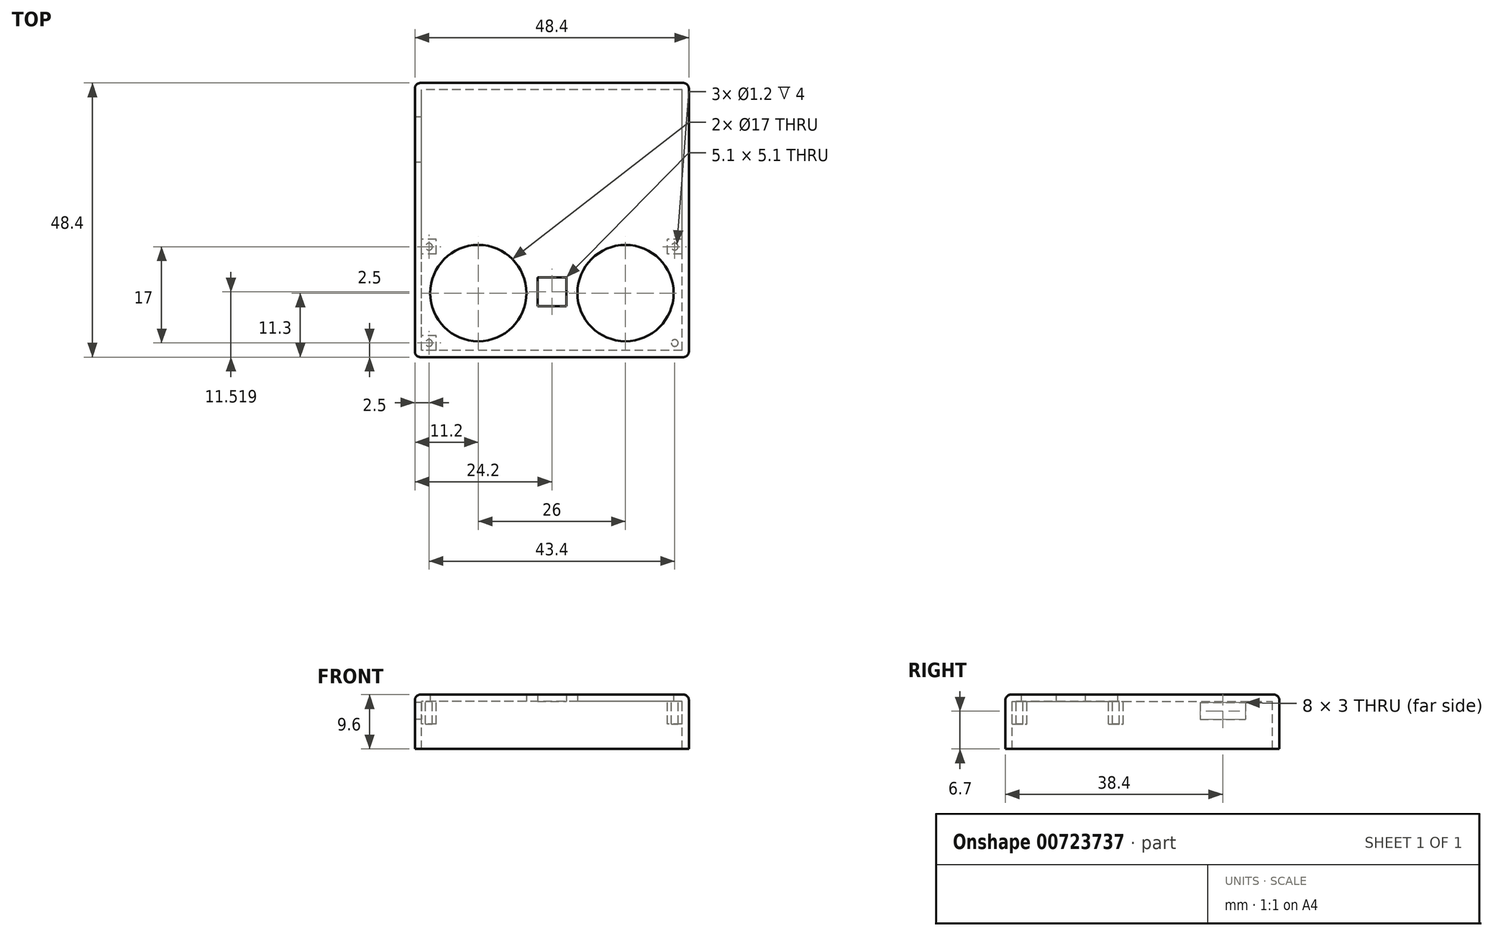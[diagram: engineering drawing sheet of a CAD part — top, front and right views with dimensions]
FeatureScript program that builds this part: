
annotation { "Feature Type Name" : "Feature", "Feature Type Description" : "" }
export const myFeature = defineFeature(function(context is Context, id is Id, definition is map)
    precondition{}
    {
        {
            var Q0;
            Q0=qCreatedBy(makeId("Top.planeOp"),FACE);
            var sketch = newSketch(context, id + "F0", { "sketchPlane" : qUnion([Q0])});
            skLineSegment(sketch, "E0.bottom", {"start": v(0, 0) * mm, "end": v(-23, 0) * mm});
            skLineSegment(sketch, "E0.top", {"start": v(0, 23) * mm, "end": v(-23, 23) * mm});
            skLineSegment(sketch, "E0.left", {"start": v(0, 0) * mm, "end": v(0, 23) * mm});
            skLineSegment(sketch, "E0.right", {"start": v(-23, 0) * mm, "end": v(-23, 23) * mm});
            skLineSegment(sketch, "E1.MirrorCS", {"start": v(-23, 0) * mm, "end": v(-23, -23) * mm});
            skLineSegment(sketch, "E2.MirrorCS", {"start": v(0, 0) * mm, "end": v(0, -23) * mm});
            skLineSegment(sketch, "E3.MirrorCS", {"start": v(0, -23) * mm, "end": v(-23, -23) * mm});
            skLineSegment(sketch, "E4.MirrorCS", {"start": v(0, 23) * mm, "end": v(23, 23) * mm});
            skLineSegment(sketch, "E5.MirrorCS", {"start": v(0, -23) * mm, "end": v(23, -23) * mm});
            skLineSegment(sketch, "E6.MirrorCS", {"start": v(23, 0) * mm, "end": v(23, 23) * mm});
            skLineSegment(sketch, "E7.MirrorCS", {"start": v(0, 0) * mm, "end": v(23, 0) * mm});
            skLineSegment(sketch, "E8.MirrorCS", {"start": v(23, 0) * mm, "end": v(23, -23) * mm});
            skCircle(sketch, "E9", {"center": v(13, -12.9) * mm, "radius": 8.5 * mm});
            skCircle(sketch, "E10", {"center": v(-13, -12.9) * mm, "radius": 8.5 * mm});
            skLineSegment(sketch, "E11.bottom", {"start": v(-2.55, -15.23) * mm, "end": v(2.55, -15.23) * mm});
            skLineSegment(sketch, "E11.top", {"start": v(-2.55, -10.13) * mm, "end": v(2.55, -10.13) * mm});
            skLineSegment(sketch, "E11.left", {"start": v(-2.55, -15.23) * mm, "end": v(-2.55, -10.13) * mm});
            skLineSegment(sketch, "E11.right", {"start": v(2.55, -15.23) * mm, "end": v(2.55, -10.13) * mm});
            skSolve(sketch);
        }
        {
            var Q0;
            {var subQ1=sQuery(id+"F0.wireOp",EDGE,"E0.top");Q0=makeQuery(id+"F0.imprint","IMPRINT",FACE,{"disambiguationData":[TD([[makeQuery(id+"F0.imprint","IMPRINT",EDGE,{"derivedFrom":subQ1}),1.0]])]});}
            var Q1;
            {var subQ1=sQuery(id+"F0.wireOp",EDGE,"E1.MirrorCS");Q1=makeQuery(id+"F0.imprint","IMPRINT",FACE,{"disambiguationData":[TD([[makeQuery(id+"F0.imprint","IMPRINT",EDGE,{"derivedFrom":subQ1}),1.0]])]});}
            var Q2;
            {var subQ7=sQuery(id+"F0.wireOp",EDGE,"E4.MirrorCS");Q2=makeQuery(id+"F0.imprint","IMPRINT",FACE,{"disambiguationData":[TD([[makeQuery(id+"F0.imprint","IMPRINT",EDGE,{"derivedFrom":subQ7}),-1.0]])]});}
            var Q3;
            {var subQ9=sQuery(id+"F0.wireOp",EDGE,"E5.MirrorCS");Q3=makeQuery(id+"F0.imprint","IMPRINT",FACE,{"disambiguationData":[TD([[makeQuery(id+"F0.imprint","IMPRINT",EDGE,{"derivedFrom":subQ9}),1.0]])]});}
            extrude(context, id + "F1", {"entities" : qUnion([Q0, Q1, Q2, Q3]), "endBound" : BoundingType.SYMMETRIC, "depth" : 1.2 * mm, "offsetDistance" : 25 * mm});
        }
        {
            var Q0;
            Q0=makeQuery(id+"F1.opExtrude","CAP_FACE",FACE,{"disambiguationData":[OSD([sQuery(id+"F0.wireOp",EDGE,"E0.top"),sQuery(id+"F0.wireOp",EDGE,"E0.right"),sQuery(id+"F0.wireOp",EDGE,"E1.MirrorCS"),sQuery(id+"F0.wireOp",EDGE,"E3.MirrorCS"),sQuery(id+"F0.wireOp",EDGE,"18OHl2Td-8SmV-nLja-3BuC-y3GKfxBrHoTz"),sQuery(id+"F0.wireOp",EDGE,"E4.MirrorCS"),sQuery(id+"F0.wireOp",EDGE,"f96b6ea1-77e4-4928-808a-502d4fa3524e1.MirrorC"),sQuery(id+"F0.wireOp",EDGE,"E5.MirrorCS"),sQuery(id+"F0.wireOp",EDGE,"E6.MirrorCS"),sQuery(id+"F0.wireOp",EDGE,"E8.MirrorCS"),sQuery(id+"F0.wireOp",EDGE,"ZzQ9hNgQ-oA48-EWd8-CxiW-ZcLfL0NBcqYF")])],"isStart":false});
            var sketch = newSketch(context, id + "F2", { "sketchPlane" : qUnion([Q0])});
            skLineSegment(sketch, "E12.0", {"start": v(23, 23) * mm, "end": v(-23, 23) * mm});
            skLineSegment(sketch, "E12.1", {"start": v(-23, -23) * mm, "end": v(-23, 23) * mm});
            skLineSegment(sketch, "E12.2", {"start": v(23, -23) * mm, "end": v(-23, -23) * mm});
            skLineSegment(sketch, "E12.3", {"start": v(23, -23) * mm, "end": v(23, 23) * mm});
            skPoint(sketch, "E12.4", {"position": v(0, 0) * mm});
            skLineSegment(sketch, "E13.bottom", {"start": v(0, 24.2) * mm, "end": v(-24.2, 24.2) * mm});
            skLineSegment(sketch, "E13.top", {"start": v(0, -24.2) * mm, "end": v(-24.2, -24.2) * mm});
            skLineSegment(sketch, "E13.left", {"start": v(0, 24.2) * mm, "end": v(0, -24.2) * mm});
            skLineSegment(sketch, "E13.right", {"start": v(-24.2, 24.2) * mm, "end": v(-24.2, -24.2) * mm});
            skLineSegment(sketch, "E14.MirrorCS", {"start": v(0, 24.2) * mm, "end": v(24.2, 24.2) * mm});
            skLineSegment(sketch, "E15.MirrorCS", {"start": v(24.2, 24.2) * mm, "end": v(24.2, -24.2) * mm});
            skLineSegment(sketch, "E16.MirrorCS", {"start": v(0, -24.2) * mm, "end": v(24.2, -24.2) * mm});
            skSolve(sketch);
        }
        {
            var Q0;
            {var subQ1=sQuery(id+"F2.wireOp",EDGE,"E12.1");Q0=makeQuery(id+"F2.imprint","IMPRINT",FACE,{"disambiguationData":[TD([[makeQuery(id+"F2.imprint","IMPRINT",EDGE,{"derivedFrom":subQ1}),1.0]])]});}
            var Q1;
            {var subQ4=sQuery(id+"F2.wireOp",EDGE,"E12.3");Q1=makeQuery(id+"F2.imprint","IMPRINT",FACE,{"disambiguationData":[TD([[makeQuery(id+"F2.imprint","IMPRINT",EDGE,{"derivedFrom":subQ4}),-1.0]])]});}
            extrude(context, id + "F3", {"entities" : qUnion([Q0, Q1]), "operationType" : NewBodyOperationType.ADD, "oppositeDirection" : true, "depth" : 9.6 * mm, "offsetDistance" : 25 * mm});
        }
        {
            var Q0;
            Q0=makeQuery(id+"F1.opExtrude","CAP_FACE",FACE,{"disambiguationData":[OSD([sQuery(id+"F0.wireOp",EDGE,"E0.top"),sQuery(id+"F0.wireOp",EDGE,"E0.right"),sQuery(id+"F0.wireOp",EDGE,"E1.MirrorCS"),sQuery(id+"F0.wireOp",EDGE,"E3.MirrorCS"),sQuery(id+"F0.wireOp",EDGE,"18OHl2Td-8SmV-nLja-3BuC-y3GKfxBrHoTz"),sQuery(id+"F0.wireOp",EDGE,"E4.MirrorCS"),sQuery(id+"F0.wireOp",EDGE,"f96b6ea1-77e4-4928-808a-502d4fa3524e1.MirrorC"),sQuery(id+"F0.wireOp",EDGE,"E5.MirrorCS"),sQuery(id+"F0.wireOp",EDGE,"E6.MirrorCS"),sQuery(id+"F0.wireOp",EDGE,"E8.MirrorCS"),sQuery(id+"F0.wireOp",EDGE,"ZzQ9hNgQ-oA48-EWd8-CxiW-ZcLfL0NBcqYF")])],"isStart":true});
            var sketch = newSketch(context, id + "F4", { "sketchPlane" : qUnion([Q0])});
            skLineSegment(sketch, "E17.0", {"start": v(23, 23) * mm, "end": v(-23, 23) * mm});
            skLineSegment(sketch, "E17.1", {"start": v(-23, 23) * mm, "end": v(-23, -23) * mm});
            skLineSegment(sketch, "E17.2", {"start": v(23, -23) * mm, "end": v(-23, -23) * mm});
            skLineSegment(sketch, "E17.3", {"start": v(23, 23) * mm, "end": v(23, -23) * mm});
            skLineSegment(sketch, "E18", {"start": v(-21.7, 23) * mm, "end": v(-21.7, 21.7) * mm, "construction": true});
            skLineSegment(sketch, "E19", {"start": v(-21.7, 21.7) * mm, "end": v(-23, 21.7) * mm, "construction": true});
            skCircle(sketch, "E20", {"center": v(-21.7, 21.7) * mm, "radius": 0.6 * mm});
            skCircle(sketch, "E21.MirrorC", {"center": v(21.7, 21.7) * mm, "radius": 0.6 * mm});
            skLineSegment(sketch, "E22.bottom", {"start": v(-20.4, 23) * mm, "end": v(-23, 23) * mm});
            skLineSegment(sketch, "E22.top", {"start": v(-20.4, 20.4) * mm, "end": v(-23, 20.4) * mm});
            skLineSegment(sketch, "E22.left", {"start": v(-20.4, 23) * mm, "end": v(-20.4, 20.4) * mm});
            skLineSegment(sketch, "E22.right", {"start": v(-23, 23) * mm, "end": v(-23, 20.4) * mm});
            skLineSegment(sketch, "E23.MirrorCS", {"start": v(20.4, 23) * mm, "end": v(20.4, 20.4) * mm});
            skLineSegment(sketch, "E24.MirrorCS", {"start": v(20.4, 20.4) * mm, "end": v(23, 20.4) * mm});
            skLineSegment(sketch, "E25", {"start": v(-21.7, 6) * mm, "end": v(-21.7, 4.7) * mm, "construction": true});
            skLineSegment(sketch, "E26", {"start": v(-21.7, 4.7) * mm, "end": v(-23, 4.7) * mm, "construction": true});
            skCircle(sketch, "E27", {"center": v(-21.7, 4.7) * mm, "radius": 0.6 * mm});
            skLineSegment(sketch, "E28.bottom", {"start": v(-20.4, 6) * mm, "end": v(-23, 6) * mm});
            skLineSegment(sketch, "E28.top", {"start": v(-20.4, 3.4) * mm, "end": v(-23, 3.4) * mm});
            skLineSegment(sketch, "E28.left", {"start": v(-20.4, 6) * mm, "end": v(-20.4, 3.4) * mm});
            skLineSegment(sketch, "E28.right", {"start": v(-23, 6) * mm, "end": v(-23, 3.4) * mm});
            skLineSegment(sketch, "E29", {"start": v(21.7, 6) * mm, "end": v(21.7, 4.7) * mm, "construction": true});
            skLineSegment(sketch, "E30", {"start": v(21.7, 4.7) * mm, "end": v(20.4, 4.7) * mm, "construction": true});
            skCircle(sketch, "E31", {"center": v(21.7, 4.7) * mm, "radius": 0.6 * mm});
            skLineSegment(sketch, "E32.bottom", {"start": v(23, 6) * mm, "end": v(20.4, 6) * mm});
            skLineSegment(sketch, "E32.top", {"start": v(23, 3.4) * mm, "end": v(20.4, 3.4) * mm});
            skLineSegment(sketch, "E32.left", {"start": v(23, 6) * mm, "end": v(23, 3.4) * mm});
            skLineSegment(sketch, "E32.right", {"start": v(20.4, 6) * mm, "end": v(20.4, 3.4) * mm});
            skSolve(sketch);
        }
        {
            var Q0;
            Q0=makeQuery(id+"F4.imprint","IMPRINT",FACE,{"disambiguationData":[TD([[makeQuery(id+"F4.imprint","IMPRINT",EDGE,{"derivedFrom":sQuery(id+"F4.wireOp",EDGE,"E21.MirrorC")}),1.0]])]});
            var Q1;
            Q1=makeQuery(id+"F4.imprint","IMPRINT",FACE,{"disambiguationData":[TD([[makeQuery(id+"F4.imprint","IMPRINT",EDGE,{"derivedFrom":sQuery(id+"F4.wireOp",EDGE,"E20")}),-1.0]])]});
            var Q2;
            Q2=makeQuery(id+"F4.imprint","IMPRINT",FACE,{"disambiguationData":[TD([[makeQuery(id+"F4.imprint","IMPRINT",EDGE,{"derivedFrom":sQuery(id+"F4.wireOp",EDGE,"E27")}),-1.0]])]});
            var Q3;
            Q3=makeQuery(id+"F4.imprint","IMPRINT",FACE,{"disambiguationData":[TD([[makeQuery(id+"F4.imprint","IMPRINT",EDGE,{"derivedFrom":sQuery(id+"F4.wireOp",EDGE,"E31")}),-1.0]])]});
            extrude(context, id + "F5", {"entities" : qUnion([Q0, Q1, Q2, Q3]), "operationType" : NewBodyOperationType.ADD, "depth" : 4 * mm, "offsetDistance" : 25 * mm});
        }
        {
            var Q0;
            Q0=makeQuery(id+"F3.opExtrude","SWEPT_FACE",FACE,{"disambiguationData":[OSD([sQuery(id+"F2.wireOp",EDGE,"E13.right")])]});
            var sketch = newSketch(context, id + "F6", { "sketchPlane" : qUnion([Q0])});
            skLineSegment(sketch, "E33.bottom", {"start": v(-18.2, -3.8) * mm, "end": v(-10.2, -3.8) * mm});
            skLineSegment(sketch, "E33.top", {"start": v(-18.2, -0.8) * mm, "end": v(-10.2, -0.8) * mm});
            skLineSegment(sketch, "E33.left", {"start": v(-18.2, -3.8) * mm, "end": v(-18.2, -0.8) * mm});
            skLineSegment(sketch, "E33.right", {"start": v(-10.2, -3.8) * mm, "end": v(-10.2, -0.8) * mm});
            skSolve(sketch);
        }
        {
            var Q0;
            Q0=qSketchRegion(id+"F6",true);
            extrude(context, id + "F7", {"entities" : qUnion([Q0]), "operationType" : NewBodyOperationType.REMOVE, "oppositeDirection" : true, "depth" : 1.4 * mm, "offsetDistance" : 25 * mm});
        }
        {
            var Q0;
            Q0=makeQuery(id+"F3.opExtrude","CAP_EDGE",EDGE,{"disambiguationData":[OSD([sQuery(id+"F2.wireOp",EDGE,"E15.MirrorCS")])],"isStart":true});
            var Q1;
            Q1=makeQuery(id+"F3.opExtrude","CAP_EDGE",EDGE,{"disambiguationData":[OSD([sQuery(id+"F2.wireOp",EDGE,"E13.right")])],"isStart":true});
            var Q2;
            Q2=makeQuery(id+"F3.opExtrude","CAP_EDGE",EDGE,{"disambiguationData":[OSD([sQuery(id+"F2.wireOp",EDGE,"E13.top"),sQuery(id+"F2.wireOp",EDGE,"E16.MirrorCS")])],"isStart":true});
            var Q3;
            Q3=makeQuery(id+"F3.opExtrude","CAP_EDGE",EDGE,{"disambiguationData":[OSD([sQuery(id+"F2.wireOp",EDGE,"E13.bottom"),sQuery(id+"F2.wireOp",EDGE,"E14.MirrorCS")])],"isStart":true});
            var Q4;
            Q4=makeQuery(id+"F3.opExtrude","SWEPT_EDGE",EDGE,{"disambiguationData":[OSD([sQuery(id+"F2.wireOp",EDGE,"E15.MirrorCS"),sQuery(id+"F2.wireOp",EDGE,"E16.MirrorCS")])]});
            var Q5;
            Q5=makeQuery(id+"F3.opExtrude","SWEPT_EDGE",EDGE,{"disambiguationData":[OSD([sQuery(id+"F2.wireOp",EDGE,"E14.MirrorCS"),sQuery(id+"F2.wireOp",EDGE,"E15.MirrorCS")])]});
            var Q6;
            Q6=makeQuery(id+"F3.opExtrude","SWEPT_EDGE",EDGE,{"disambiguationData":[OSD([sQuery(id+"F2.wireOp",EDGE,"E13.top"),sQuery(id+"F2.wireOp",EDGE,"E13.right")])]});
            var Q7;
            Q7=makeQuery(id+"F3.opExtrude","SWEPT_EDGE",EDGE,{"disambiguationData":[OSD([sQuery(id+"F2.wireOp",EDGE,"E13.bottom"),sQuery(id+"F2.wireOp",EDGE,"E13.right")])]});
            fillet(context, id + "F8", {"entities" : qUnion([Q0, Q1, Q2, Q3, Q4, Q5, Q6, Q7]), "radius" : 1 * mm, "tangentPropagation" : true, "allowEdgeOverflow" : false});
        }
    });
